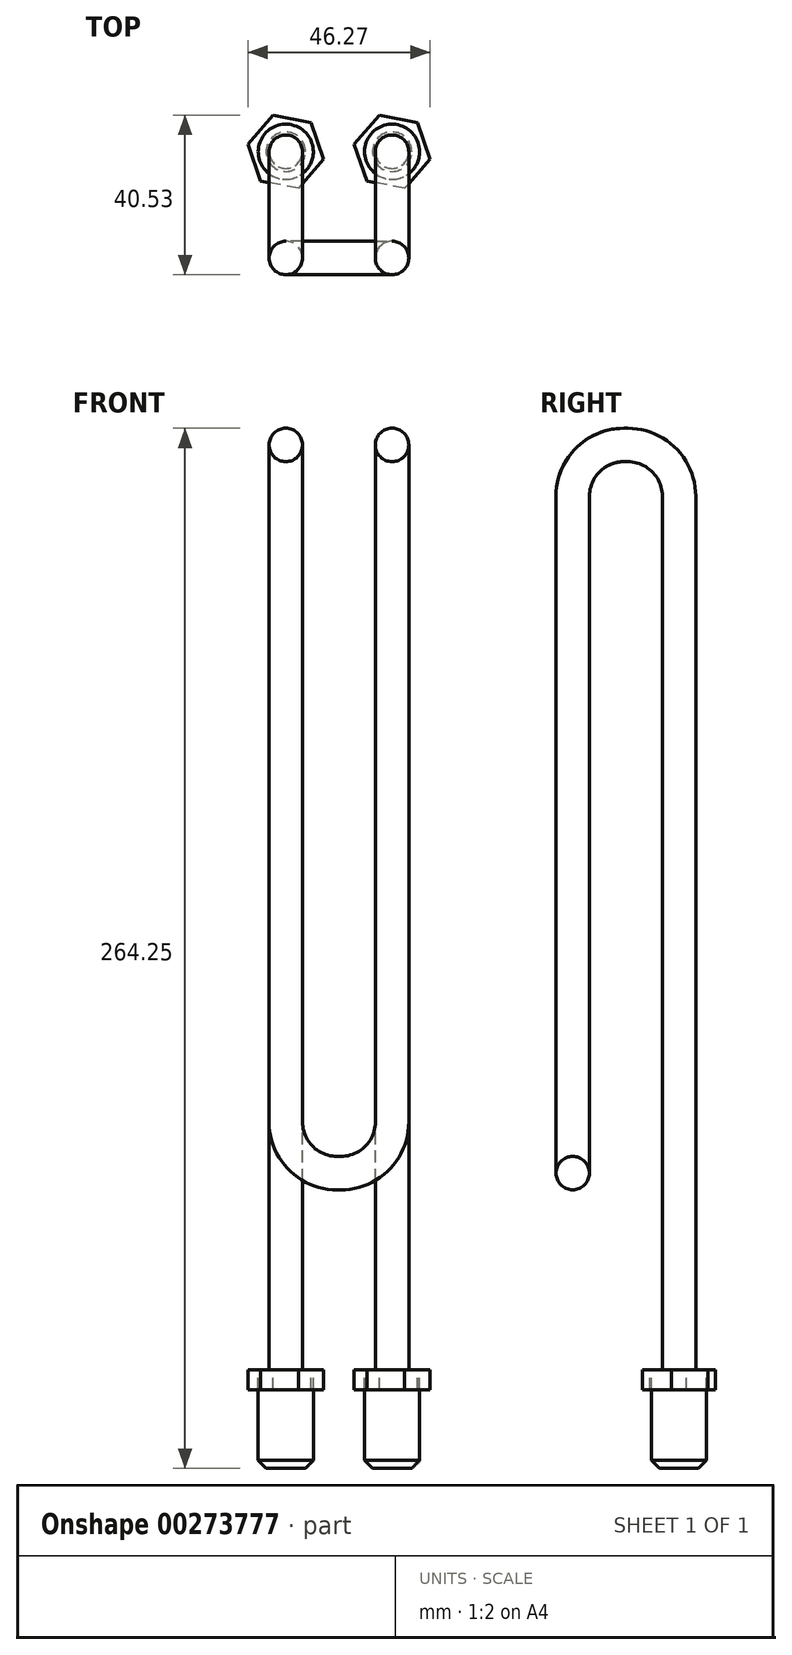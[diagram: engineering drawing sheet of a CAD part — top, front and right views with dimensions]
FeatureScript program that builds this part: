
annotation { "Feature Type Name" : "Feature", "Feature Type Description" : "" }
export const myFeature = defineFeature(function(context is Context, id is Id, definition is map)
    precondition{}
    {
        {
            var Q0;
            Q0=qCreatedBy(makeId("Front.planeOp"),FACE);
            var sketch = newSketch(context, id + "F0", { "sketchPlane" : qUnion([Q0])});
            skLineSegment(sketch, "E0", {"start": v(-13.5, 0) * mm, "end": v(-13.5, 222) * mm});
            skSolve(sketch);
        }
        {
            var Q0;
            Q0=sQuery(id+"F0.wireOp",EDGE,"E0");
            var Q1;
            Q1=qCreatedBy(makeId("Right.planeOp"),FACE);
            cPlane(context, id + "F1", {"entities" : qUnion([Q0, Q1]), "cplaneType" : CPlaneType.LINE_ANGLE, "offset" : 0 * mm, "angle" : 0 * degree, "width" : 150 * mm, "height" : 150 * mm});
        }
        {
            var Q0;
            Q0=qCreatedBy(id+"F1.planeOp",FACE);
            var sketch = newSketch(context, id + "F2", { "sketchPlane" : qUnion([Q0])});
            skLineSegment(sketch, "E1", {"start": v(13, 235) * mm, "end": v(14, 235) * mm});
            skLineSegment(sketch, "E2", {"start": v(27, 222) * mm, "end": v(27, 68.64) * mm});
            skLineSegment(sketch, "E3", {"start": v(0, 222) * mm, "end": v(0, 222) * mm});
            skPoint(sketch, "E4.visualSharp", {"position": v(27, 235) * mm});
            skArc(sketch, "E4.filletArc", {"start": v(27, 222) * mm, "mid": v(23.2, 231.2) * mm, "end": v(14, 235) * mm});
            skPoint(sketch, "E5.visualSharp", {"position": v(0, 235) * mm});
            skArc(sketch, "E5.filletArc", {"start": v(13, 235) * mm, "mid": v(3.8, 231.2) * mm, "end": v(0, 222) * mm});
            skSolve(sketch);
        }
        {
            var Q0;
            Q0=qCreatedBy(makeId("Top.planeOp"),FACE);
            var sketch = newSketch(context, id + "F3", { "sketchPlane" : qUnion([Q0])});
            skCircle(sketch, "E6", {"center": v(-13.5, 0) * mm, "radius": 4.25 * mm});
            skSolve(sketch);
        }
        {
            var Q0;
            Q0=sQuery(id+"F2.wireOp",EDGE,"E2");
            var Q1;
            Q1=qCreatedBy(makeId("Front.planeOp"),FACE);
            cPlane(context, id + "F4", {"entities" : qUnion([Q0, Q1]), "cplaneType" : CPlaneType.LINE_ANGLE, "offset" : 25 * mm, "angle" : 0 * degree, "width" : 150 * mm, "height" : 150 * mm});
        }
        {
            var Q0;
            Q0=qCreatedBy(id+"F4.planeOp",FACE);
            var sketch = newSketch(context, id + "F5", { "sketchPlane" : qUnion([Q0])});
            skLineSegment(sketch, "E7", {"start": v(13.5, 68.64) * mm, "end": v(13.5, 63) * mm});
            skLineSegment(sketch, "E8", {"start": v(0.5, 50) * mm, "end": v(0, 50) * mm});
            skPoint(sketch, "E9.visualSharp", {"position": v(13.5, 50) * mm});
            skArc(sketch, "E9.filletArc", {"start": v(0.5, 50) * mm, "mid": v(9.7, 53.8) * mm, "end": v(13.5, 63) * mm});
            skSolve(sketch);
        }
        {
            var Q0;
            Q0=makeQuery(id+"F3.imprint","IMPRINT",FACE,{"disambiguationData":[TD([[makeQuery(id+"F3.imprint","IMPRINT",EDGE,{"derivedFrom":sQuery(id+"F3.wireOp",EDGE,"E6")}),1.0]])]});
            var Q1;
            Q1=sQuery(id+"F0.wireOp",EDGE,"E0");
            sweep(context, id + "F6", {"profiles" : qUnion([Q0]), "path" : qUnion([Q1])});
        }
        {
            var Q0;
            Q0=makeQuery(id+"F6.opSweep","CAP_FACE",FACE,{"disambiguationData":[OSD([sQuery(id+"F0.wireOp",VERTEX,"E0.end"),sQuery(id+"F3.wireOp",EDGE,"E6")])],"isStart":false});
            var Q1;
            Q1=sQuery(id+"F2.wireOp",EDGE,"E5.filletArc");
            var Q2;
            Q2=sQuery(id+"F2.wireOp",EDGE,"E1");
            var Q3;
            Q3=sQuery(id+"F2.wireOp",EDGE,"E4.filletArc");
            var Q4;
            Q4=sQuery(id+"F2.wireOp",EDGE,"E2");
            var Q5;
            Q5=sQuery(id+"F5.wireOp",EDGE,"E7");
            var Q6;
            Q6=sQuery(id+"F5.wireOp",EDGE,"E9.filletArc");
            var Q7;
            Q7=sQuery(id+"F5.wireOp",EDGE,"E8");
            sweep(context, id + "F7", {"operationType" : NewBodyOperationType.ADD, "profiles" : qUnion([Q0]), "path" : qUnion([Q1, Q2, Q3, Q4, Q5, Q6, Q7])});
        }
        {
            var Q0;
            Q0=makeQuery(id+"F6.opSweep","SWEPT_BODY",BODY,{"disambiguationData":[OSD([sQuery(id+"F0.wireOp",EDGE,"E0"),sQuery(id+"F3.wireOp",EDGE,"E6")])]});
            var Q1;
            Q1=qCreatedBy(makeId("Right.planeOp"),FACE);
            mirror(context, id + "F8", {"operationType" : NewBodyOperationType.ADD, "entities" : qUnion([Q0]), "mirrorPlane" : qUnion([Q1])});
        }
        {
            var Q0;
            Q0=qCreatedBy(makeId("Top.planeOp"),FACE);
            var sketch = newSketch(context, id + "F9", { "sketchPlane" : qUnion([Q0])});
            skCircle(sketch, "E10.cCircle", {"center": v(-13.5, 0) * mm, "radius": 8.5 * mm, "construction": true});
            skLineSegment(sketch, "E10.0", {"start": v(-16.7, 9.28) * mm, "end": v(-7.06, 7.41) * mm});
            skLineSegment(sketch, "E10.1", {"start": v(-7.06, 7.41) * mm, "end": v(-3.86, -1.87) * mm});
            skLineSegment(sketch, "E10.2", {"start": v(-3.86, -1.87) * mm, "end": v(-10.3, -9.28) * mm});
            skLineSegment(sketch, "E10.3", {"start": v(-10.3, -9.28) * mm, "end": v(-19.93, -7.41) * mm});
            skLineSegment(sketch, "E10.4", {"start": v(-19.93, -7.41) * mm, "end": v(-23.13, 1.87) * mm});
            skLineSegment(sketch, "E10.5", {"start": v(-23.13, 1.87) * mm, "end": v(-16.7, 9.28) * mm});
            skPoint(sketch, "E10.0.midPoint", {"position": v(-11.88, 8.35) * mm});
            skCircle(sketch, "E11.cCircle", {"center": v(13.5, 0) * mm, "radius": 8.5 * mm, "construction": true});
            skLineSegment(sketch, "E11.0", {"start": v(10.3, 9.28) * mm, "end": v(19.93, 7.41) * mm});
            skLineSegment(sketch, "E11.1", {"start": v(19.93, 7.41) * mm, "end": v(23.14, -1.87) * mm});
            skLineSegment(sketch, "E11.2", {"start": v(23.14, -1.87) * mm, "end": v(16.7, -9.28) * mm});
            skLineSegment(sketch, "E11.3", {"start": v(16.7, -9.28) * mm, "end": v(7.07, -7.41) * mm});
            skLineSegment(sketch, "E11.4", {"start": v(7.07, -7.41) * mm, "end": v(3.86, 1.87) * mm});
            skLineSegment(sketch, "E11.5", {"start": v(3.86, 1.87) * mm, "end": v(10.3, 9.28) * mm});
            skPoint(sketch, "E11.0.midPoint", {"position": v(15.12, 8.35) * mm});
            skSolve(sketch);
        }
        {
            var Q0;
            Q0=makeQuery(id+"F9.imprint","IMPRINT",FACE,{"disambiguationData":[TD([[makeQuery(id+"F9.imprint","IMPRINT",EDGE,{"derivedFrom":sQuery(id+"F9.wireOp",EDGE,"E10.0")}),-1.0]])]});
            var Q1;
            Q1=makeQuery(id+"F9.imprint","IMPRINT",FACE,{"disambiguationData":[TD([[makeQuery(id+"F9.imprint","IMPRINT",EDGE,{"derivedFrom":sQuery(id+"F9.wireOp",EDGE,"E11.0")}),-1.0]])]});
            extrude(context, id + "F10", {"entities" : qUnion([Q0, Q1]), "oppositeDirection" : true, "depth" : 5 * mm});
        }
        {
            var Q0;
            Q0=qCreatedBy(makeId("Top.planeOp"),FACE);
            var sketch = newSketch(context, id + "F11", { "sketchPlane" : qUnion([Q0])});
            skCircle(sketch, "E12", {"center": v(-13.5, 0) * mm, "radius": 7 * mm});
            skCircle(sketch, "E13", {"center": v(13.5, 0) * mm, "radius": 7 * mm});
            skSolve(sketch);
        }
        {
            var Q0;
            Q0 = qSketchRegion(id + "F11", true);
            extrude(context, id + "F12", {"entities" : qUnion([Q0]), "oppositeDirection" : true, "depth" : 25 * mm});
        }
        {
            var Q0;
            Q0=makeQuery(id+"F12.opExtrude","CAP_EDGE",EDGE,{"disambiguationData":[OSD([sQuery(id+"F11.wireOp",EDGE,"E12")])],"isStart":false});
            var Q1;
            Q1=makeQuery(id+"F12.opExtrude","CAP_EDGE",EDGE,{"disambiguationData":[OSD([sQuery(id+"F11.wireOp",EDGE,"E13")])],"isStart":false});
            chamfer(context, id + "F13", {"entities" : qUnion([Q0, Q1]), "width" : 2 * mm, "tangentPropagation" : true});
        }
    });
